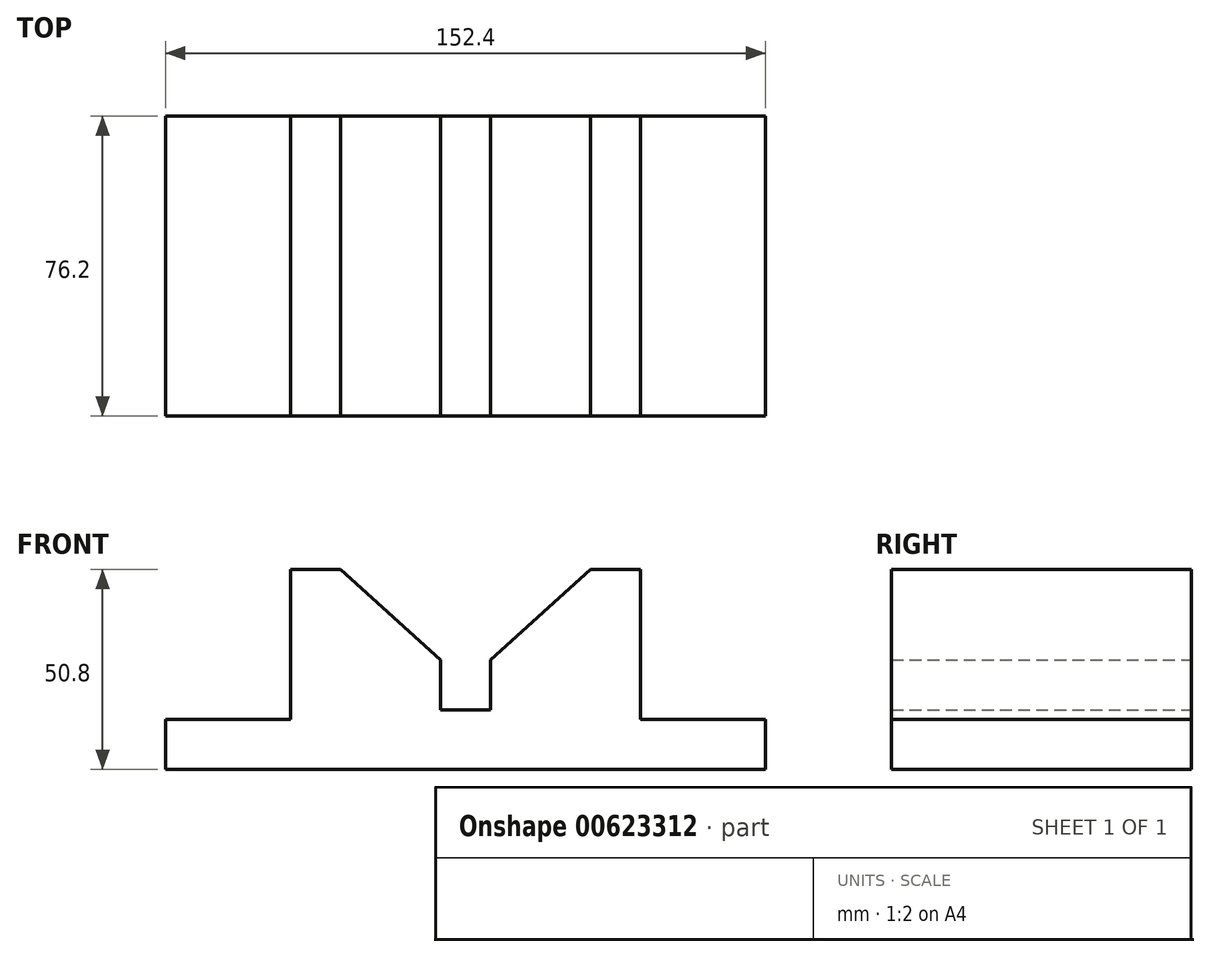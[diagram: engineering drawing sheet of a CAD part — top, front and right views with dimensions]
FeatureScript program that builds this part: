
annotation { "Feature Type Name" : "Feature", "Feature Type Description" : "" }
export const myFeature = defineFeature(function(context is Context, id is Id, definition is map)
    precondition{}
    {
        {
            var Q0;
            Q0=qCreatedBy(makeId("Front.planeOp"),FACE);
            var sketch = newSketch(context, id + "F0", { "sketchPlane" : qUnion([Q0])});
            skLineSegment(sketch, "E0", {"start": v(0, 0) * mm, "end": v(152.4, 0) * mm});
            skLineSegment(sketch, "E1", {"start": v(152.4, 0) * mm, "end": v(152.4, 12.7) * mm});
            skLineSegment(sketch, "E2", {"start": v(152.4, 12.7) * mm, "end": v(120.65, 12.7) * mm});
            skLineSegment(sketch, "E3", {"start": v(120.65, 12.7) * mm, "end": v(120.65, 50.8) * mm});
            skLineSegment(sketch, "E4", {"start": v(120.65, 50.8) * mm, "end": v(107.95, 50.8) * mm});
            skLineSegment(sketch, "E5", {"start": v(44.45, 50.8) * mm, "end": v(31.75, 50.8) * mm});
            skLineSegment(sketch, "E6", {"start": v(31.75, 50.8) * mm, "end": v(31.75, 12.7) * mm});
            skLineSegment(sketch, "E7", {"start": v(31.75, 12.7) * mm, "end": v(0, 12.7) * mm});
            skLineSegment(sketch, "E8", {"start": v(0, 12.7) * mm, "end": v(0, 0) * mm});
            skLineSegment(sketch, "E9", {"start": v(44.45, 50.8) * mm, "end": v(69.85, 27.76) * mm});
            skLineSegment(sketch, "E10", {"start": v(69.85, 27.76) * mm, "end": v(69.85, 15.06) * mm});
            skLineSegment(sketch, "E11", {"start": v(69.85, 15.06) * mm, "end": v(82.55, 15.06) * mm});
            skLineSegment(sketch, "E12", {"start": v(82.55, 15.06) * mm, "end": v(82.55, 27.76) * mm});
            skLineSegment(sketch, "E13", {"start": v(82.55, 27.76) * mm, "end": v(107.95, 50.8) * mm});
            skSolve(sketch);
        }
        {
            var Q0;
            Q0 = qSketchRegion(id + "F0", true);
            extrude(context, id + "F1", {"entities" : qUnion([Q0]), "depth" : 76.2 * mm, "offsetDistance" : 25.4 * mm});
        }
    });
